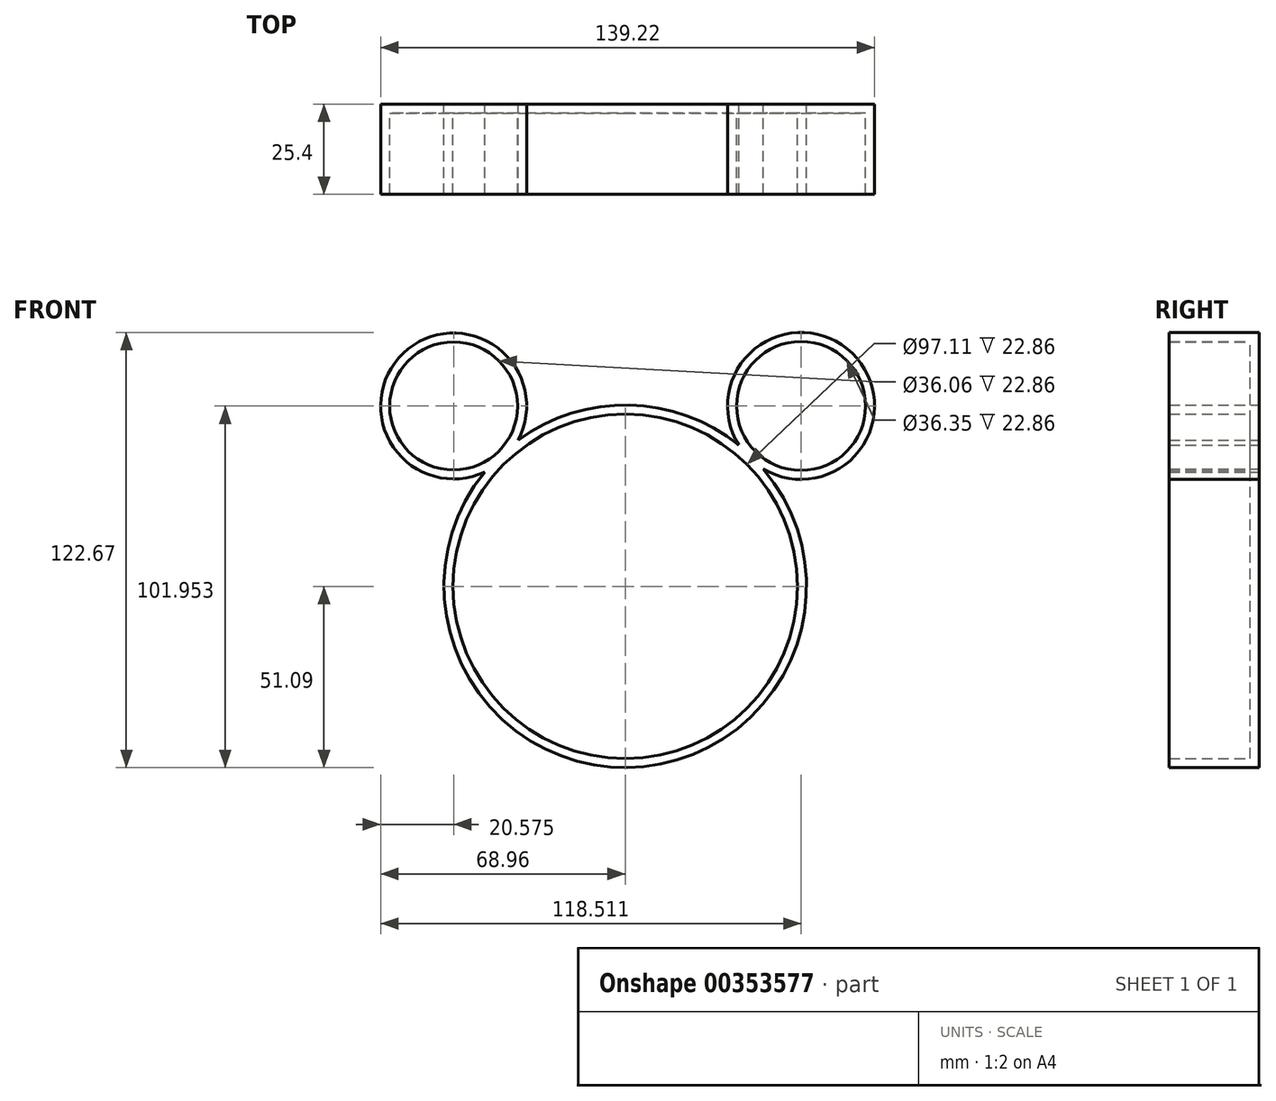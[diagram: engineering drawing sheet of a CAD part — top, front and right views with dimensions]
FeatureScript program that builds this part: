
annotation { "Feature Type Name" : "Feature", "Feature Type Description" : "" }
export const myFeature = defineFeature(function(context is Context, id is Id, definition is map)
    precondition{}
    {
        {
            var Q0;
            Q0=qCreatedBy(makeId("Front.planeOp"),FACE);
            var sketch = newSketch(context, id + "F0", { "sketchPlane" : qUnion([Q0])});
            skCircle(sketch, "E0", {"center": v(0, 0) * mm, "radius": 51.1 * mm});
            skCircle(sketch, "E1", {"center": v(-48.38, 50.86) * mm, "radius": 20.57 * mm});
            skCircle(sketch, "E2", {"center": v(49.55, 50.86) * mm, "radius": 20.71 * mm});
            skSolve(sketch);
        }
        {
            var Q0;
            Q0 = qSketchRegion(id + "F0", true);
            extrude(context, id + "F1", {"entities" : qUnion([Q0]), "depth" : 25.4 * mm});
        }
        {
            var Q0;
            Q0=makeQuery(id+"F1.opExtrude","CAP_FACE",FACE,{"disambiguationData":[OSD([sQuery(id+"F0.wireOp",EDGE,"E0"),sQuery(id+"F0.wireOp",EDGE,"E1"),sQuery(id+"F0.wireOp",EDGE,"E2")])],"isStart":false});
            shell(context, id + "F2", {"entities" : qUnion([Q0]), "thickness" : 2.54 * mm});
        }
    });
